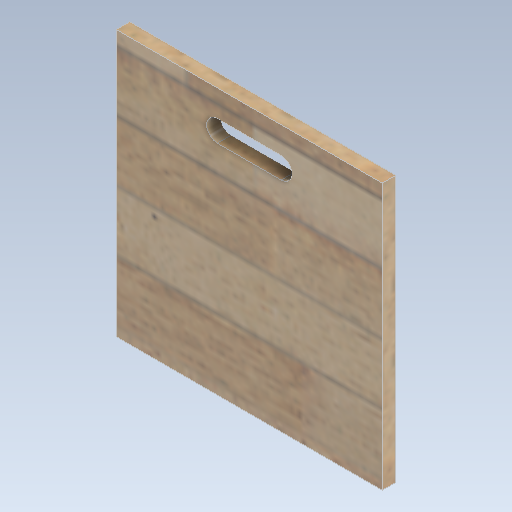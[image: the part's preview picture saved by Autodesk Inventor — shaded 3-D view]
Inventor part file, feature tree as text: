
AUTODESK INVENTOR PART (.ipt)
format: ipt  version: 2021 (Build 250183000, 183)  size: 244,224 bytes
history: native  units: mm
features: extrude x2, sketch x2
ambient origin geometry x8: Origin, YZ Plane, XZ Plane, XY Plane, X Axis, Y Axis, Z Axis, Center Point
bodies: Solid1 (feature_tree)
feature tree (4):
  extrude  "Extrusion1"  Depth=30.0mm
  extrude  "Extrusion2"  Depth=25.0mm
  sketch  "Sketch1"  dims[d3=0.0mm d4=30.0mm]
  sketch  "Sketch2"  dims[d5=20.0mm d6=25.0mm d7=12.7mm d8=0.0mm]
